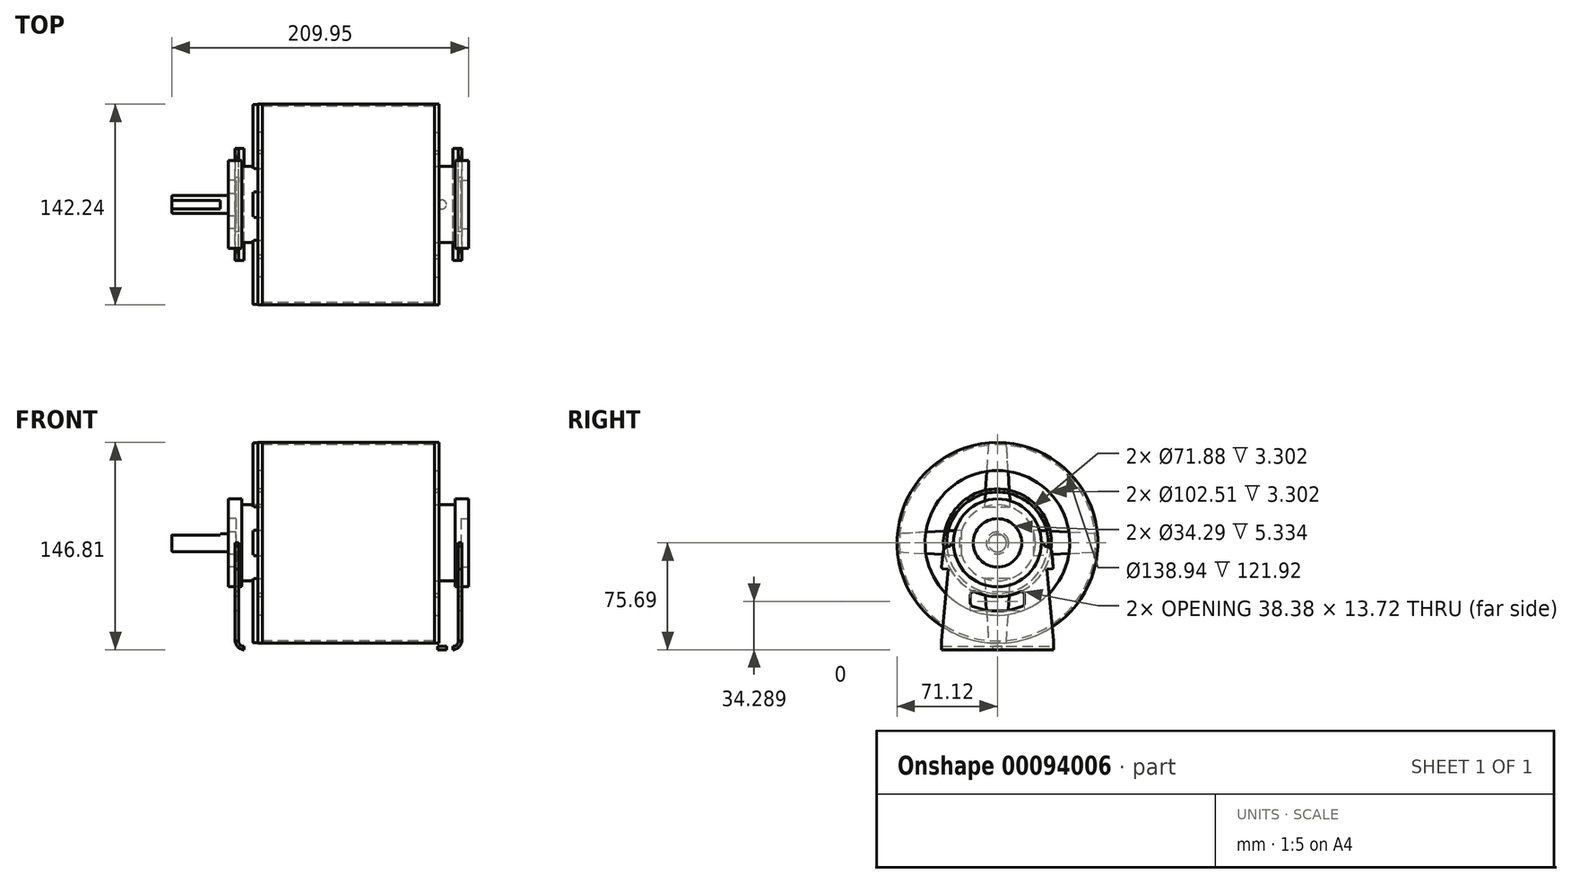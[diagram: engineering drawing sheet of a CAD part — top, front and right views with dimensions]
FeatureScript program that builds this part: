
annotation { "Feature Type Name" : "Feature", "Feature Type Description" : "" }
export const myFeature = defineFeature(function(context is Context, id is Id, definition is map)
    precondition{}
    {
        {
            var Q0;
            Q0=qCreatedBy(makeId("Right.planeOp"),FACE);
            var sketch = newSketch(context, id + "F0", { "sketchPlane" : qUnion([Q0])});
            skCircle(sketch, "E0", {"center": v(0, 0) * mm, "radius": 71.12 * mm});
            skCircle(sketch, "E1.0", {"center": v(0, 0) * mm, "radius": 69.47 * mm});
            skSolve(sketch);
        }
        {
            var Q0;
            Q0=makeQuery(id+"F0.imprint","IMPRINT",FACE,{"disambiguationData":[TD([[makeQuery(id+"F0.imprint","IMPRINT",EDGE,{"derivedFrom":sQuery(id+"F0.wireOp",EDGE,"E0")}),1.0]])]});
            extrude(context, id + "F1", {"entities" : qUnion([Q0]), "depth" : 121.92 * mm});
        }
        {
            var Q0;
            Q0=qCreatedBy(makeId("Front.planeOp"),FACE);
            var sketch = newSketch(context, id + "F2", { "sketchPlane" : qUnion([Q0])});
            skLineSegment(sketch, "E2", {"start": v(0, 0) * mm, "end": v(0, 71.12) * mm});
            skLineSegment(sketch, "E3", {"start": v(0, 71.12) * mm, "end": v(-3.3, 71.12) * mm});
            skLineSegment(sketch, "E4", {"start": v(-3.3, 71.12) * mm, "end": v(-3.3, 26.92) * mm});
            skLineSegment(sketch, "E5", {"start": v(-3.3, 26.92) * mm, "end": v(-14.48, 26.92) * mm});
            skLineSegment(sketch, "E6", {"start": v(-14.48, 26.92) * mm, "end": v(-14.48, 31.12) * mm});
            skLineSegment(sketch, "E7", {"start": v(-14.48, 31.12) * mm, "end": v(-24, 31.12) * mm});
            skLineSegment(sketch, "E8", {"start": v(-24, 31.12) * mm, "end": v(-24, 17.15) * mm});
            skLineSegment(sketch, "E9", {"start": v(-24, 17.15) * mm, "end": v(-18.67, 17.15) * mm});
            skLineSegment(sketch, "E10", {"start": v(-18.67, 17.15) * mm, "end": v(-18.67, 0) * mm});
            skLineSegment(sketch, "E11", {"start": v(-18.67, 0) * mm, "end": v(0, 0) * mm});
            skSolve(sketch);
        }
        {
            var Q0;
            Q0=makeQuery(id+"F2.imprint","IMPRINT",FACE,{"disambiguationData":[TD([[makeQuery(id+"F2.imprint","IMPRINT",EDGE,{"derivedFrom":sQuery(id+"F2.wireOp",EDGE,"E2")}),1.0]])]});
            var Q1;
            Q1=sQuery(id+"F2.wireOp",EDGE,"E11");
            revolve(context, id + "F3", {"entities" : qUnion([Q0]), "axis" : qUnion([Q1]), "revolveType" : RevolveType.FULL});
        }
        {
            var Q0;
            Q0=makeQuery(id+"F3.opRevolve","SWEPT_FACE",FACE,{"disambiguationData":[OSD([sQuery(id+"F2.wireOp",EDGE,"E4")])]});
            var sketch = newSketch(context, id + "F4", { "sketchPlane" : qUnion([Q0])});
            skCircle(sketch, "E12", {"center": v(0, 0) * mm, "radius": 51.26 * mm});
            skCircle(sketch, "E13", {"center": v(0, 0) * mm, "radius": 38.23 * mm});
            skCircle(sketch, "E14.0", {"center": v(0, 0) * mm, "radius": 35.94 * mm});
            skSolve(sketch);
        }
        {
            var Q0;
            Q0=qSketchRegion(id+"F4",true);
            var Q1;
            Q1=makeQuery(id+"F4.imprint","IMPRINT",FACE,{"disambiguationData":[TD([[makeQuery(id+"F4.imprint","IMPRINT",EDGE,{"derivedFrom":sQuery(id+"F4.wireOp",EDGE,"E14.0")}),1.0]])]});
            extrude(context, id + "F5", {"entities" : qUnion([Q0, Q1]), "operationType" : NewBodyOperationType.REMOVE, "endBound" : BoundingType.THROUGH_ALL, "oppositeDirection" : true, "depth" : 25.4 * mm});
        }
        {
            var Q0;
            Q0=qCreatedBy(makeId("Right.planeOp"),FACE);
            var sketch = newSketch(context, id + "F6", { "sketchPlane" : qUnion([Q0])});
            skLineSegment(sketch, "E15", {"start": v(0, 0) * mm, "end": v(0, 71.12) * mm, "construction": true});
            skPoint(sketch, "E16.rect.middle", {"position": v(0, 71.12) * mm});
            skCircle(sketch, "E17", {"center": v(0, 26.92) * mm, "radius": 9.2 * mm, "construction": true});
            skCircle(sketch, "E18.0", {"center": v(0, 0) * mm, "radius": 71.12 * mm, "construction": true});
            skCircle(sketch, "E19", {"center": v(0, 71.12) * mm, "radius": 6.35 * mm, "construction": true});
            skLineSegment(sketch, "E20", {"start": v(9.07, 25.35) * mm, "end": v(6.38, 70.83) * mm});
            skLineSegment(sketch, "E21", {"start": v(6.38, 70.83) * mm, "end": v(-6.38, 70.83) * mm});
            skLineSegment(sketch, "E22", {"start": v(-6.38, 70.83) * mm, "end": v(-9.07, 25.35) * mm});
            skLineSegment(sketch, "E23", {"start": v(-9.07, 25.35) * mm, "end": v(9.07, 25.35) * mm});
            skCircle(sketch, "E24.0", {"center": v(0, 0) * mm, "radius": 26.92 * mm, "construction": true});
            skSolve(sketch);
        }
        {
            var Q0;
            {var subQ3=sQuery(id+"F6.wireOp",EDGE,"E20");Q0=makeQuery(id+"F6.imprint","IMPRINT",FACE,{"disambiguationData":[TD([[makeQuery(id+"F6.imprint","IMPRINT",EDGE,{"derivedFrom":subQ3}),1.0]])]});}
            extrude(context, id + "F7", {"entities" : qUnion([Q0]), "oppositeDirection" : true, "depth" : 6.6 * mm});
        }
        {
            var Q0;
            Q0=makeQuery(id+"F7.opExtrude","CAP_EDGE",EDGE,{"disambiguationData":[OSD([sQuery(id+"F6.wireOp",EDGE,"E20")])],"isStart":false});
            var Q1;
            Q1=makeQuery(id+"F7.opExtrude","CAP_EDGE",EDGE,{"disambiguationData":[OSD([sQuery(id+"F6.wireOp",EDGE,"E21")])],"isStart":false});
            var Q2;
            Q2=makeQuery(id+"F7.opExtrude","CAP_EDGE",EDGE,{"disambiguationData":[OSD([sQuery(id+"F6.wireOp",EDGE,"E22")])],"isStart":false});
            var Q3;
            Q3=makeQuery(id+"F7.opExtrude","SWEPT_EDGE",EDGE,{"disambiguationData":[OSD([sQuery(id+"F2.wireOp",EDGE,"E3"),sQuery(id+"F2.wireOp",EDGE,"E4"),sQuery(id+"F6.wireOp",EDGE,"E20"),sQuery(id+"F6.wireOp",EDGE,"E21")])]});
            var Q4;
            Q4=makeQuery(id+"F7.opExtrude","SWEPT_EDGE",EDGE,{"disambiguationData":[OSD([sQuery(id+"F2.wireOp",EDGE,"E3"),sQuery(id+"F2.wireOp",EDGE,"E4"),sQuery(id+"F6.wireOp",EDGE,"E21"),sQuery(id+"F6.wireOp",EDGE,"E22")])]});
            fillet(context, id + "F8", {"entities" : qUnion([Q0, Q1, Q2, Q3, Q4]), "radius" : 0.5 * mm, "tangentPropagation" : true, "allowEdgeOverflow" : false});
        }
        {
            var Q0;
            Q0=makeQuery(id+"F7.opExtrude","SWEPT_BODY",BODY,{"disambiguationData":[OSD([sQuery(id+"F2.wireOp",EDGE,"E4"),sQuery(id+"F2.wireOp",EDGE,"E5"),sQuery(id+"F6.wireOp",EDGE,"E20"),sQuery(id+"F6.wireOp",EDGE,"E21"),sQuery(id+"F6.wireOp",EDGE,"E22")])]});
            var Q1;
            Q1=sQuery(id+"F2.wireOp",EDGE,"E11");
            circularPattern(context, id + "F9", {"entities" : qUnion([Q0]), "axis" : qUnion([Q1]), "angle" : 360 * degree, "instanceCount" : 4, "equalSpace" : true});
        }
        {
            var Q0;
            Q0=qCreatedBy(makeId("Right.planeOp"),FACE);
            cPlane(context, id + "F10", {"entities" : qUnion([Q0]), "cplaneType" : CPlaneType.OFFSET, "offset" : 60.96 * mm, "width" : 152.4 * mm, "height" : 152.4 * mm});
        }
        {
            var Q0;
            Q0=makeQuery(id+"F5.boolean.opBoolean","SPLIT",BODY,{"disambiguationData":[OD(0.0)],"derivedFrom":makeQuery(id+"F3.opRevolve","SWEPT_BODY",BODY,{"disambiguationData":[OSD([sQuery(id+"F2.wireOp",EDGE,"E2"),sQuery(id+"F2.wireOp",EDGE,"E3"),sQuery(id+"F2.wireOp",EDGE,"E4"),sQuery(id+"F2.wireOp",EDGE,"E5"),sQuery(id+"F2.wireOp",EDGE,"E6"),sQuery(id+"F2.wireOp",EDGE,"E7"),sQuery(id+"F2.wireOp",EDGE,"E8"),sQuery(id+"F2.wireOp",EDGE,"E9"),sQuery(id+"F2.wireOp",EDGE,"E10"),sQuery(id+"F2.wireOp",EDGE,"E11")])]})});
            var Q1;
            Q1=qCreatedBy(id+"F10.planeOp",FACE);
            mirror(context, id + "F11", {"entities" : qUnion([Q0]), "mirrorPlane" : qUnion([Q1])});
        }
        {
            var Q0;
            Q0=qCreatedBy(makeId("Front.planeOp"),FACE);
            var sketch = newSketch(context, id + "F12", { "sketchPlane" : qUnion([Q0])});
            skLineSegment(sketch, "E25.0.0", {"start": v(-18.67, -17.15) * mm, "end": v(-18.67, 17.15) * mm, "construction": true});
            skLineSegment(sketch, "E26", {"start": v(-18.67, 0) * mm, "end": v(-64.03, 0) * mm});
            skLineSegment(sketch, "E27", {"start": v(-64.03, 0) * mm, "end": v(-64.03, 5.84) * mm});
            skLineSegment(sketch, "E28", {"start": v(-63.53, 6.35) * mm, "end": v(-23.75, 6.35) * mm});
            skLineSegment(sketch, "E29", {"start": v(-23.24, 7.89) * mm, "end": v(-18.67, 7.89) * mm});
            skLineSegment(sketch, "E30", {"start": v(-18.67, 7.89) * mm, "end": v(-18.67, 0) * mm});
            skLineSegment(sketch, "E31", {"start": v(-23.75, 7.38) * mm, "end": v(-23.75, 6.35) * mm});
            skPoint(sketch, "E32.visualSharp", {"position": v(-23.75, 7.89) * mm});
            skArc(sketch, "E32.filletArc", {"start": v(-23.24, 7.89) * mm, "mid": v(-23.6, 7.74) * mm, "end": v(-23.75, 7.38) * mm});
            skPoint(sketch, "E33.visualSharp", {"position": v(-64.03, 6.35) * mm});
            skArc(sketch, "E33.filletArc", {"start": v(-63.53, 6.35) * mm, "mid": v(-63.88, 6.2) * mm, "end": v(-64.03, 5.84) * mm});
            skSolve(sketch);
        }
        {
            var Q0;
            Q0=makeQuery(id+"F12.imprint","IMPRINT",FACE,{"disambiguationData":[TD([[makeQuery(id+"F12.imprint","IMPRINT",EDGE,{"derivedFrom":sQuery(id+"F12.wireOp",EDGE,"E26")}),-1.0]])]});
            var Q1;
            Q1=sQuery(id+"F12.wireOp",EDGE,"E26");
            revolve(context, id + "F13", {"entities" : qUnion([Q0]), "axis" : qUnion([Q1]), "revolveType" : RevolveType.FULL});
        }
        {
            var Q0;
            Q0=makeQuery(id+"F13.opRevolve","SWEPT_FACE",FACE,{"disambiguationData":[OSD([sQuery(id+"F12.wireOp",EDGE,"E27")])]});
            var sketch = newSketch(context, id + "F14", { "sketchPlane" : qUnion([Q0])});
            skCircle(sketch, "E34.0", {"center": v(0, 0) * mm, "radius": 6.35 * mm});
            skLineSegment(sketch, "E35", {"start": v(-6.6, -6.35) * mm, "end": v(6.6, -6.35) * mm, "construction": true});
            skLineSegment(sketch, "E36", {"start": v(0, -6.35) * mm, "end": v(0, 6.35) * mm, "construction": true});
            skLineSegment(sketch, "E37.0", {"start": v(-3.02, 5.59) * mm, "end": v(3.02, 5.59) * mm});
            skSolve(sketch);
        }
        {
            var Q0;
            {var subQ0=makeQuery(id+"F13.opRevolve","SWEPT_EDGE",EDGE,{"disambiguationData":[OSD([sQuery(id+"F12.wireOp",EDGE,"E27"),sQuery(id+"F12.wireOp",EDGE,"E33.filletArc")])]});var subQ1=sQuery(id+"F14.wireOp",EDGE,"E37.0");var subQ3=makeQuery(id+"F14.imprint","INTERSECT",VERTEX,{"disambiguationData":[OD(0.0)],"derivedFrom":[subQ0,subQ1]});Q0=makeQuery(id+"F14.imprint","IMPRINT",FACE,{"disambiguationData":[TD([[makeQuery(id+"F14.imprint","IMPRINT",EDGE,{"disambiguationData":[TD([[subQ3,-1.0]])],"derivedFrom":subQ1}),1.0]])]});}
            var Q1;
            {var subQ1=sQuery(id+"F14.wireOp",EDGE,"E37.0");var subQ4=sQuery(id+"F14.wireOp",EDGE,"E34.0");var subQ6=makeQuery(id+"F14.imprint","INTERSECT",VERTEX,{"disambiguationData":[OD(0.0)],"derivedFrom":[subQ4,subQ1]});Q1=makeQuery(id+"F14.imprint","IMPRINT",FACE,{"disambiguationData":[TD([[makeQuery(id+"F14.imprint","IMPRINT",EDGE,{"disambiguationData":[TD([[subQ6,1.0]])],"derivedFrom":subQ4}),1.0]])]});}
            extrude(context, id + "F15", {"entities" : qUnion([Q0, Q1]), "operationType" : NewBodyOperationType.REMOVE, "oppositeDirection" : true, "depth" : 34.04 * mm});
        }
        {
            var Q0;
            Q0=qCreatedBy(makeId("Front.planeOp"),FACE);
            var sketch = newSketch(context, id + "F16", { "sketchPlane" : qUnion([Q0])});
            skLineSegment(sketch, "E38", {"start": v(-154.25, 0) * mm, "end": v(252.33, 0) * mm, "construction": true});
            skLineSegment(sketch, "E39", {"start": v(-12.9, -75.7) * mm, "end": v(134.81, -75.7) * mm});
            skLineSegment(sketch, "E40", {"start": v(-24, 31.12) * mm, "end": v(-14.48, 31.12) * mm, "construction": true});
            skLineSegment(sketch, "E41", {"start": v(136.4, 31.12) * mm, "end": v(145.92, 31.12) * mm, "construction": true});
            skLineSegment(sketch, "E42", {"start": v(-19.24, 31.12) * mm, "end": v(-19.24, 0) * mm, "construction": true});
            skLineSegment(sketch, "E43", {"start": v(141.16, 31.12) * mm, "end": v(141.16, 0) * mm, "construction": true});
            skLineSegment(sketch, "E44", {"start": v(-19.24, 0) * mm, "end": v(-19.24, -69.34) * mm});
            skLineSegment(sketch, "E45", {"start": v(141.16, 0) * mm, "end": v(141.16, -69.34) * mm});
            skPoint(sketch, "E46.visualSharp", {"position": v(-19.24, -75.7) * mm});
            skArc(sketch, "E46.filletArc", {"start": v(-19.24, -69.34) * mm, "mid": v(-17.38, -73.83) * mm, "end": v(-12.9, -75.7) * mm});
            skPoint(sketch, "E47.visualSharp", {"position": v(141.16, -75.7) * mm});
            skArc(sketch, "E47.filletArc", {"start": v(134.81, -75.7) * mm, "mid": v(139.3, -73.83) * mm, "end": v(141.16, -69.34) * mm});
            skLineSegment(sketch, "E48.0", {"start": v(138.87, 0) * mm, "end": v(138.87, -69.34) * mm});
            skArc(sketch, "E48.1", {"start": v(134.81, -73.4) * mm, "mid": v(137.68, -72.22) * mm, "end": v(138.87, -69.34) * mm});
            skLineSegment(sketch, "E48.2", {"start": v(-12.9, -73.4) * mm, "end": v(134.81, -73.4) * mm});
            skArc(sketch, "E48.3", {"start": v(-16.95, -69.34) * mm, "mid": v(-15.76, -72.22) * mm, "end": v(-12.9, -73.4) * mm});
            skLineSegment(sketch, "E48.4", {"start": v(-16.95, 0) * mm, "end": v(-16.95, -69.34) * mm});
            skLineSegment(sketch, "E49", {"start": v(-19.24, 0) * mm, "end": v(-16.95, 0) * mm});
            skLineSegment(sketch, "E50", {"start": v(138.87, 0) * mm, "end": v(141.16, 0) * mm});
            skSolve(sketch);
        }
        {
            var Q0;
            Q0=qSketchRegion(id+"F16",true);
            extrude(context, id + "F17", {"entities" : qUnion([Q0]), "endBound" : BoundingType.SYMMETRIC, "depth" : 79.5 * mm});
        }
        {
            var Q0;
            Q0=qCreatedBy(makeId("Top.planeOp"),FACE);
            cPlane(context, id + "F18", {"entities" : qUnion([Q0]), "cplaneType" : CPlaneType.OFFSET, "offset" : 75.7 * mm, "oppositeDirection" : true, "width" : 152.4 * mm, "height" : 152.4 * mm});
        }
        {
            var Q0;
            Q0=qCreatedBy(id+"F18.planeOp",FACE);
            var sketch = newSketch(context, id + "F19", { "sketchPlane" : qUnion([Q0])});
            skLineSegment(sketch, "E51.0", {"start": v(-19.24, -39.75) * mm, "end": v(-12.9, -39.75) * mm, "construction": true});
            skLineSegment(sketch, "E52.0", {"start": v(-19.24, 39.75) * mm, "end": v(-12.9, 39.75) * mm, "construction": true});
            skLineSegment(sketch, "E53.bottom", {"start": v(15.34, 66.04) * mm, "end": v(15.34, 66.04) * mm});
            skLineSegment(sketch, "E53.top", {"start": v(15.34, 40.64) * mm, "end": v(15.34, 40.64) * mm});
            skLineSegment(sketch, "E53.left", {"start": v(11.37, 62.07) * mm, "end": v(11.37, 44.6) * mm});
            skLineSegment(sketch, "E53.right", {"start": v(19.3, 62.07) * mm, "end": v(19.3, 44.6) * mm});
            skPoint(sketch, "E54.visualSharp", {"position": v(11.37, 66.04) * mm});
            skArc(sketch, "E54.filletArc", {"start": v(15.34, 66.04) * mm, "mid": v(12.53, 64.88) * mm, "end": v(11.37, 62.07) * mm});
            skPoint(sketch, "E55.visualSharp", {"position": v(19.3, 66.04) * mm});
            skArc(sketch, "E55.filletArc", {"start": v(19.3, 62.07) * mm, "mid": v(18.14, 64.88) * mm, "end": v(15.34, 66.04) * mm});
            skPoint(sketch, "E56.visualSharp", {"position": v(19.3, 40.64) * mm});
            skArc(sketch, "E56.filletArc", {"start": v(15.34, 40.64) * mm, "mid": v(18.14, 41.8) * mm, "end": v(19.3, 44.6) * mm});
            skPoint(sketch, "E57.visualSharp", {"position": v(11.37, 40.64) * mm});
            skArc(sketch, "E57.filletArc", {"start": v(11.37, 44.6) * mm, "mid": v(12.53, 41.8) * mm, "end": v(15.34, 40.64) * mm});
            skLineSegment(sketch, "E58", {"start": v(2.98, 39.75) * mm, "end": v(2.98, -39.75) * mm, "construction": true});
            skLineSegment(sketch, "E59", {"start": v(-19.24, 0) * mm, "end": v(141.16, 0) * mm, "construction": true});
            skLineSegment(sketch, "E60", {"start": v(9.33, 71.5) * mm, "end": v(111.68, 71.5) * mm});
            skLineSegment(sketch, "E61", {"start": v(9.33, -71.5) * mm, "end": v(111.68, -71.5) * mm});
            skLineSegment(sketch, "E62", {"start": v(2.98, 46.1) * mm, "end": v(2.98, 65.15) * mm});
            skLineSegment(sketch, "E63", {"start": v(2.98, -46.1) * mm, "end": v(2.98, -65.15) * mm});
            skLineSegment(sketch, "E64", {"start": v(-19.24, 39.75) * mm, "end": v(-19.24, -39.75) * mm, "construction": true});
            skLineSegment(sketch, "E65.0", {"start": v(141.16, -39.75) * mm, "end": v(141.16, 39.75) * mm, "construction": true});
            skLineSegment(sketch, "E66", {"start": v(141.16, 39.75) * mm, "end": v(134.81, 39.75) * mm, "construction": true});
            skLineSegment(sketch, "E67", {"start": v(126.25, 45.4) * mm, "end": v(117.6, 67.47) * mm});
            skPoint(sketch, "E68.visualSharp", {"position": v(128.46, 39.75) * mm});
            skArc(sketch, "E68.filletArc", {"start": v(126.25, 45.4) * mm, "mid": v(129.51, 41.3) * mm, "end": v(134.52, 39.75) * mm});
            skPoint(sketch, "E69.visualSharp", {"position": v(2.98, 71.5) * mm});
            skArc(sketch, "E69.filletArc", {"start": v(9.33, 71.5) * mm, "mid": v(4.84, 69.64) * mm, "end": v(2.98, 65.15) * mm});
            skLineSegment(sketch, "E70.0.MirrorCS", {"start": v(141.16, -39.75) * mm, "end": v(134.81, -39.75) * mm, "construction": true});
            skLineSegment(sketch, "E70.1.MirrorCS", {"start": v(126.25, -45.4) * mm, "end": v(117.6, -67.47) * mm});
            skArc(sketch, "E70.2.MirrorCS", {"start": v(126.25, -45.4) * mm, "mid": v(129.51, -41.3) * mm, "end": v(134.52, -39.75) * mm});
            skPoint(sketch, "E71.visualSharp", {"position": v(116.01, 71.5) * mm});
            skArc(sketch, "E71.filletArc", {"start": v(117.6, 67.47) * mm, "mid": v(115.26, 70.4) * mm, "end": v(111.68, 71.5) * mm});
            skPoint(sketch, "E72.visualSharp", {"position": v(116.01, -71.5) * mm});
            skArc(sketch, "E72.filletArc", {"start": v(111.68, -71.5) * mm, "mid": v(115.26, -70.4) * mm, "end": v(117.6, -67.47) * mm});
            skPoint(sketch, "E73.visualSharp", {"position": v(2.98, -71.5) * mm});
            skArc(sketch, "E73.filletArc", {"start": v(2.98, -65.15) * mm, "mid": v(4.84, -69.64) * mm, "end": v(9.33, -71.5) * mm});
            skPoint(sketch, "E74.visualSharp", {"position": v(2.98, 39.75) * mm});
            skArc(sketch, "E74.filletArc", {"start": v(-3.37, 39.75) * mm, "mid": v(1.12, 41.61) * mm, "end": v(2.98, 46.1) * mm});
            skPoint(sketch, "E75.visualSharp", {"position": v(2.98, -39.75) * mm});
            skArc(sketch, "E75.filletArc", {"start": v(2.98, -46.1) * mm, "mid": v(1.12, -41.61) * mm, "end": v(-3.37, -39.75) * mm});
            skArc(sketch, "E76.0.1.0", {"start": v(15.34, -66.04) * mm, "mid": v(18.14, -64.88) * mm, "end": v(19.3, -62.07) * mm});
            skArc(sketch, "E76.0.1.1", {"start": v(11.37, -62.07) * mm, "mid": v(12.53, -64.88) * mm, "end": v(15.34, -66.04) * mm});
            skLineSegment(sketch, "E76.0.1.2", {"start": v(11.37, -44.6) * mm, "end": v(11.37, -62.07) * mm});
            skArc(sketch, "E76.0.1.3", {"start": v(15.34, -40.64) * mm, "mid": v(12.53, -41.8) * mm, "end": v(11.37, -44.6) * mm});
            skArc(sketch, "E76.0.1.4", {"start": v(19.3, -44.6) * mm, "mid": v(18.14, -41.8) * mm, "end": v(15.34, -40.64) * mm});
            skLineSegment(sketch, "E76.0.1.5", {"start": v(19.3, -44.6) * mm, "end": v(19.3, -62.07) * mm});
            skArc(sketch, "E76.1.0.0", {"start": v(83.92, 40.64) * mm, "mid": v(86.72, 41.8) * mm, "end": v(87.88, 44.6) * mm});
            skArc(sketch, "E76.1.0.1", {"start": v(79.95, 44.6) * mm, "mid": v(81.1, 41.8) * mm, "end": v(83.92, 40.64) * mm});
            skLineSegment(sketch, "E76.1.0.2", {"start": v(79.95, 62.07) * mm, "end": v(79.95, 44.6) * mm});
            skArc(sketch, "E76.1.0.3", {"start": v(83.92, 66.04) * mm, "mid": v(81.1, 64.88) * mm, "end": v(79.95, 62.07) * mm});
            skArc(sketch, "E76.1.0.4", {"start": v(87.88, 62.07) * mm, "mid": v(86.72, 64.88) * mm, "end": v(83.92, 66.04) * mm});
            skLineSegment(sketch, "E76.1.0.5", {"start": v(87.88, 62.07) * mm, "end": v(87.88, 44.6) * mm});
            skArc(sketch, "E76.1.1.0", {"start": v(83.92, -66.04) * mm, "mid": v(86.72, -64.88) * mm, "end": v(87.88, -62.07) * mm});
            skArc(sketch, "E76.1.1.1", {"start": v(79.95, -62.07) * mm, "mid": v(81.1, -64.88) * mm, "end": v(83.92, -66.04) * mm});
            skLineSegment(sketch, "E76.1.1.2", {"start": v(79.95, -44.6) * mm, "end": v(79.95, -62.07) * mm});
            skArc(sketch, "E76.1.1.3", {"start": v(83.92, -40.64) * mm, "mid": v(81.1, -41.8) * mm, "end": v(79.95, -44.6) * mm});
            skArc(sketch, "E76.1.1.4", {"start": v(87.88, -44.6) * mm, "mid": v(86.72, -41.8) * mm, "end": v(83.92, -40.64) * mm});
            skLineSegment(sketch, "E76.1.1.5", {"start": v(87.88, -44.6) * mm, "end": v(87.88, -62.07) * mm});
            skLineSegment(sketch, "E76.direction1", {"start": v(15.34, 40.64) * mm, "end": v(83.92, 40.64) * mm, "construction": true});
            skLineSegment(sketch, "E76.direction2", {"start": v(15.34, 40.64) * mm, "end": v(15.34, -66.04) * mm, "construction": true});
            skLineSegment(sketch, "E77.0", {"start": v(-12.9, -39.75) * mm, "end": v(-12.9, 39.75) * mm});
            skLineSegment(sketch, "E78.0", {"start": v(134.81, -39.75) * mm, "end": v(134.81, 39.75) * mm});
            skLineSegment(sketch, "E79", {"start": v(-12.9, 39.75) * mm, "end": v(-3.37, 39.75) * mm});
            skLineSegment(sketch, "E80", {"start": v(-12.9, -39.75) * mm, "end": v(-3.37, -39.75) * mm});
            skLineSegment(sketch, "E81", {"start": v(134.81, 39.75) * mm, "end": v(134.52, 39.75) * mm});
            skLineSegment(sketch, "E82", {"start": v(134.81, -39.75) * mm, "end": v(134.52, -39.75) * mm});
            skSolve(sketch);
        }
        {
            var Q0;
            Q0=makeQuery(id+"F19.imprint","IMPRINT",FACE,{"disambiguationData":[TD([[makeQuery(id+"F19.imprint","IMPRINT",EDGE,{"derivedFrom":sQuery(id+"F19.wireOp",EDGE,"E53.left")}),-1.0]])]});
            extrude(context, id + "F20", {"entities" : qUnion([Q0]), "operationType" : NewBodyOperationType.ADD, "depth" : 2.3 * mm});
        }
        {
            var Q0;
            Q0=makeQuery(id+"F17.opExtrude","SWEPT_FACE",FACE,{"disambiguationData":[OSD([sQuery(id+"F16.wireOp",EDGE,"E44")])]});
            var sketch = newSketch(context, id + "F21", { "sketchPlane" : qUnion([Q0])});
            skArc(sketch, "E83.0", {"start": v(-31.12, 0) * mm, "mid": v(0, -31.12) * mm, "end": v(31.12, 0) * mm});
            skLineSegment(sketch, "E84.0", {"start": v(39.75, -69.34) * mm, "end": v(-39.75, -69.34) * mm});
            skLineSegment(sketch, "E85", {"start": v(31.87, 0) * mm, "end": v(31.12, 0) * mm});
            skLineSegment(sketch, "E86", {"start": v(-33.13, -1.15) * mm, "end": v(-39.75, -69.34) * mm});
            skLineSegment(sketch, "E87", {"start": v(33.13, -1.15) * mm, "end": v(39.75, -69.34) * mm});
            skPoint(sketch, "E88.end.orphan", {"position": v(-39.75, 0) * mm});
            skPoint(sketch, "E89.0.start.orphan", {"position": v(39.75, 0) * mm});
            skLineSegment(sketch, "E90.trimOffspring", {"start": v(-31.12, 0) * mm, "end": v(-31.87, 0) * mm});
            skLineSegment(sketch, "E91", {"start": v(0, 0) * mm, "end": v(0, -69.34) * mm, "construction": true});
            skPoint(sketch, "E92.visualSharp", {"position": v(-33.02, 0) * mm});
            skArc(sketch, "E92.filletArc", {"start": v(-31.87, 0) * mm, "mid": v(-32.72, -0.33) * mm, "end": v(-33.13, -1.15) * mm});
            skPoint(sketch, "E93.visualSharp", {"position": v(33.02, 0) * mm});
            skArc(sketch, "E93.filletArc", {"start": v(33.13, -1.15) * mm, "mid": v(32.72, -0.33) * mm, "end": v(31.87, 0) * mm});
            skLineSegment(sketch, "E94.bottom", {"start": v(33.27, -2.6) * mm, "end": v(33.78, -2.55) * mm});
            skLineSegment(sketch, "E94.top", {"start": v(34.84, -18.78) * mm, "end": v(38.38, -18.44) * mm});
            skLineSegment(sketch, "E94.left", {"start": v(33.27, -2.6) * mm, "end": v(34.84, -18.78) * mm});
            skLineSegment(sketch, "E94.right", {"start": v(38.5, -6.43) * mm, "end": v(39.52, -17.05) * mm});
            skPoint(sketch, "E95.visualSharp", {"position": v(38.08, -2.13) * mm});
            skArc(sketch, "E95.filletArc", {"start": v(38.5, -6.43) * mm, "mid": v(36.94, -3.51) * mm, "end": v(33.78, -2.55) * mm});
            skPoint(sketch, "E96.visualSharp", {"position": v(39.65, -18.31) * mm});
            skArc(sketch, "E96.filletArc", {"start": v(38.38, -18.44) * mm, "mid": v(39.24, -17.98) * mm, "end": v(39.52, -17.05) * mm});
            skLineSegment(sketch, "E97.0.MirrorCS", {"start": v(-33.27, -2.6) * mm, "end": v(-33.78, -2.55) * mm});
            skArc(sketch, "E97.1.MirrorCS", {"start": v(-38.5, -6.43) * mm, "mid": v(-36.94, -3.51) * mm, "end": v(-33.78, -2.55) * mm});
            skLineSegment(sketch, "E97.2.MirrorCS", {"start": v(-34.84, -18.78) * mm, "end": v(-38.38, -18.44) * mm});
            skLineSegment(sketch, "E97.3.MirrorCS", {"start": v(-38.5, -6.43) * mm, "end": v(-39.52, -17.05) * mm});
            skArc(sketch, "E97.4.MirrorCS", {"start": v(-38.38, -18.44) * mm, "mid": v(-39.24, -17.98) * mm, "end": v(-39.52, -17.05) * mm});
            skArc(sketch, "E98", {"start": v(-15.6, -34.76) * mm, "mid": v(0, -38.1) * mm, "end": v(15.6, -34.76) * mm});
            skArc(sketch, "E99.0", {"start": v(-17.57, -44.95) * mm, "mid": v(0, -48.26) * mm, "end": v(17.57, -44.95) * mm});
            skLineSegment(sketch, "E100.rect.left", {"start": v(19.19, -37.07) * mm, "end": v(19.19, -42.58) * mm});
            skLineSegment(sketch, "E100.rect.right", {"start": v(-19.19, -37.07) * mm, "end": v(-19.19, -42.58) * mm});
            skPoint(sketch, "E100.rect.middle", {"position": v(0, -43.18) * mm});
            skPoint(sketch, "E101.orphan", {"position": v(-19.19, -53.44) * mm});
            skPoint(sketch, "E100.rect.top.start.orphan", {"position": v(19.19, -53.44) * mm});
            skPoint(sketch, "E102.visualSharp", {"position": v(-19.19, -44.28) * mm});
            skArc(sketch, "E102.filletArc", {"start": v(-19.19, -42.58) * mm, "mid": v(-18.75, -44.01) * mm, "end": v(-17.57, -44.95) * mm});
            skPoint(sketch, "E103.visualSharp", {"position": v(19.19, -44.28) * mm});
            skArc(sketch, "E103.filletArc", {"start": v(17.57, -44.95) * mm, "mid": v(18.75, -44.01) * mm, "end": v(19.19, -42.58) * mm});
            skPoint(sketch, "E104.visualSharp", {"position": v(19.19, -32.92) * mm});
            skArc(sketch, "E104.filletArc", {"start": v(19.19, -37.07) * mm, "mid": v(18.03, -34.94) * mm, "end": v(15.6, -34.76) * mm});
            skPoint(sketch, "E105.visualSharp", {"position": v(-19.19, -32.92) * mm});
            skArc(sketch, "E105.filletArc", {"start": v(-15.6, -34.76) * mm, "mid": v(-18.03, -34.94) * mm, "end": v(-19.19, -37.07) * mm});
            skSolve(sketch);
        }
        {
            var Q0;
            {var subQ2=sQuery(id+"F21.wireOp",EDGE,"E92.filletArc");Q0=makeQuery(id+"F21.imprint","IMPRINT",FACE,{"disambiguationData":[TD([[makeQuery(id+"F21.imprint","IMPRINT",EDGE,{"derivedFrom":subQ2}),-1.0]])]});}
            var Q1;
            {var subQ2=sQuery(id+"F21.wireOp",EDGE,"E93.filletArc");Q1=makeQuery(id+"F21.imprint","IMPRINT",FACE,{"disambiguationData":[TD([[makeQuery(id+"F21.imprint","IMPRINT",EDGE,{"derivedFrom":subQ2}),-1.0]])]});}
            var Q2;
            {var subQ1=sQuery(id+"F21.wireOp",EDGE,"E83.0");Q2=makeQuery(id+"F21.imprint","IMPRINT",FACE,{"disambiguationData":[TD([[makeQuery(id+"F21.imprint","IMPRINT",EDGE,{"derivedFrom":subQ1}),1.0]])]});}
            var Q3;
            Q3=makeQuery(id+"F21.imprint","IMPRINT",FACE,{"disambiguationData":[TD([[makeQuery(id+"F21.imprint","IMPRINT",EDGE,{"derivedFrom":sQuery(id+"F21.wireOp",EDGE,"E98")}),-1.0]])]});
            extrude(context, id + "F22", {"entities" : qUnion([Q0, Q1, Q2, Q3]), "oppositeDirection" : true, "depth" : 160.4 * mm});
        }
        {
            var Q0;
            Q0=makeQuery(id+"F22.opExtrude","SWEPT_BODY",BODY,{"disambiguationData":[OSD([sQuery(id+"F16.wireOp",EDGE,"E44"),sQuery(id+"F16.wireOp",EDGE,"E49"),sQuery(id+"F21.wireOp",EDGE,"E83.0")])]});
            var Q1;
            Q1=makeQuery(id+"F22.opExtrude","SWEPT_BODY",BODY,{"disambiguationData":[OSD([sQuery(id+"F16.wireOp",EDGE,"E44"),sQuery(id+"F16.wireOp",EDGE,"E49"),sQuery(id+"F21.wireOp",EDGE,"E86"),sQuery(id+"F21.wireOp",EDGE,"E92.filletArc"),sQuery(id+"F21.wireOp",EDGE,"E97.0.MirrorCS"),sQuery(id+"F21.wireOp",EDGE,"E97.1.MirrorCS"),sQuery(id+"F21.wireOp",EDGE,"E97.2.MirrorCS"),sQuery(id+"F21.wireOp",EDGE,"E97.3.MirrorCS"),sQuery(id+"F21.wireOp",EDGE,"E97.4.MirrorCS")])]});
            var Q2;
            Q2=makeQuery(id+"F22.opExtrude","SWEPT_BODY",BODY,{"disambiguationData":[OSD([sQuery(id+"F16.wireOp",EDGE,"E44"),sQuery(id+"F16.wireOp",EDGE,"E49"),sQuery(id+"F21.wireOp",EDGE,"E87"),sQuery(id+"F21.wireOp",EDGE,"E93.filletArc"),sQuery(id+"F21.wireOp",EDGE,"E94.bottom"),sQuery(id+"F21.wireOp",EDGE,"E94.top"),sQuery(id+"F21.wireOp",EDGE,"E94.right"),sQuery(id+"F21.wireOp",EDGE,"E95.filletArc"),sQuery(id+"F21.wireOp",EDGE,"E96.filletArc")])]});
            var Q3;
            Q3=makeQuery(id+"F22.opExtrude","SWEPT_BODY",BODY,{"disambiguationData":[OSD([sQuery(id+"F21.wireOp",EDGE,"E98"),sQuery(id+"F21.wireOp",EDGE,"E99.0"),sQuery(id+"F21.wireOp",EDGE,"E100.rect.left"),sQuery(id+"F21.wireOp",EDGE,"E100.rect.right"),sQuery(id+"F21.wireOp",EDGE,"E102.filletArc"),sQuery(id+"F21.wireOp",EDGE,"E103.filletArc"),sQuery(id+"F21.wireOp",EDGE,"E104.filletArc"),sQuery(id+"F21.wireOp",EDGE,"E105.filletArc")])]});
            var Q4;
            Q4=makeQuery(id+"F17.opExtrude","SWEPT_BODY",BODY,{"disambiguationData":[OSD([sQuery(id+"F16.wireOp",EDGE,"E39"),sQuery(id+"F16.wireOp",EDGE,"E44"),sQuery(id+"F16.wireOp",EDGE,"E45"),sQuery(id+"F16.wireOp",EDGE,"E46.filletArc"),sQuery(id+"F16.wireOp",EDGE,"E47.filletArc"),sQuery(id+"F16.wireOp",EDGE,"E48.0"),sQuery(id+"F16.wireOp",EDGE,"E48.1"),sQuery(id+"F16.wireOp",EDGE,"E48.2"),sQuery(id+"F16.wireOp",EDGE,"E48.3"),sQuery(id+"F16.wireOp",EDGE,"E48.4"),sQuery(id+"F16.wireOp",EDGE,"E49"),sQuery(id+"F16.wireOp",EDGE,"E50")])]});
            booleanBodies(context, id + "F23", {"operationType" : BooleanOperationType.SUBTRACTION, "tools" : qUnion([Q0, Q1, Q2, Q3]), "targets" : qUnion([Q4])});
        }
        {
            var Q0;
            Q0=makeQuery(id+"F20.boolean.opBoolean","MERGE",FACE,{"derivedFrom":[makeQuery(id+"F17.opExtrude","SWEPT_FACE",FACE,{"disambiguationData":[OSD([sQuery(id+"F16.wireOp",EDGE,"E48.2")])]}),makeQuery(id+"F20.opExtrude","CAP_FACE",FACE,{"disambiguationData":[OSD([sQuery(id+"F19.wireOp",EDGE,"E53.left"),sQuery(id+"F19.wireOp",EDGE,"E53.right"),sQuery(id+"F19.wireOp",EDGE,"E54.filletArc"),sQuery(id+"F19.wireOp",EDGE,"E55.filletArc"),sQuery(id+"F19.wireOp",EDGE,"E56.filletArc"),sQuery(id+"F19.wireOp",EDGE,"E57.filletArc"),sQuery(id+"F19.wireOp",EDGE,"E60"),sQuery(id+"F19.wireOp",EDGE,"E61"),sQuery(id+"F19.wireOp",EDGE,"E62"),sQuery(id+"F19.wireOp",EDGE,"E63"),sQuery(id+"F19.wireOp",EDGE,"E67"),sQuery(id+"F19.wireOp",EDGE,"E68.filletArc"),sQuery(id+"F19.wireOp",EDGE,"E69.filletArc"),sQuery(id+"F19.wireOp",EDGE,"E70.1.MirrorCS"),sQuery(id+"F19.wireOp",EDGE,"E70.2.MirrorCS"),sQuery(id+"F19.wireOp",EDGE,"E71.filletArc"),sQuery(id+"F19.wireOp",EDGE,"E72.filletArc"),sQuery(id+"F19.wireOp",EDGE,"E73.filletArc"),sQuery(id+"F19.wireOp",EDGE,"E74.filletArc"),sQuery(id+"F19.wireOp",EDGE,"E75.filletArc"),sQuery(id+"F19.wireOp",EDGE,"E76.0.1.0"),sQuery(id+"F19.wireOp",EDGE,"E76.0.1.1"),sQuery(id+"F19.wireOp",EDGE,"E76.0.1.2"),sQuery(id+"F19.wireOp",EDGE,"E76.0.1.3"),sQuery(id+"F19.wireOp",EDGE,"E76.0.1.4"),sQuery(id+"F19.wireOp",EDGE,"E76.0.1.5"),sQuery(id+"F19.wireOp",EDGE,"E76.1.0.0"),sQuery(id+"F19.wireOp",EDGE,"E76.1.0.1"),sQuery(id+"F19.wireOp",EDGE,"E76.1.0.2"),sQuery(id+"F19.wireOp",EDGE,"E76.1.0.3"),sQuery(id+"F19.wireOp",EDGE,"E76.1.0.4"),sQuery(id+"F19.wireOp",EDGE,"E76.1.0.5"),sQuery(id+"F19.wireOp",EDGE,"E76.1.1.0"),sQuery(id+"F19.wireOp",EDGE,"E76.1.1.1"),sQuery(id+"F19.wireOp",EDGE,"E76.1.1.2"),sQuery(id+"F19.wireOp",EDGE,"E76.1.1.3"),sQuery(id+"F19.wireOp",EDGE,"E76.1.1.4"),sQuery(id+"F19.wireOp",EDGE,"E76.1.1.5"),sQuery(id+"F19.wireOp",EDGE,"E77.0"),sQuery(id+"F19.wireOp",EDGE,"E78.0"),sQuery(id+"F19.wireOp",EDGE,"E79"),sQuery(id+"F19.wireOp",EDGE,"E80"),sQuery(id+"F19.wireOp",EDGE,"E81"),sQuery(id+"F19.wireOp",EDGE,"E82")])],"isStart":false})]});
            var sketch = newSketch(context, id + "F24", { "sketchPlane" : qUnion([Q0])});
            skLineSegment(sketch, "E106.0", {"start": v(-12.9, -39.75) * mm, "end": v(-12.9, 39.75) * mm, "construction": true});
            skLineSegment(sketch, "E107.0", {"start": v(134.81, -39.75) * mm, "end": v(134.81, 39.75) * mm, "construction": true});
            skLineSegment(sketch, "E108.rect.bottom", {"start": v(4.89, 7.62) * mm, "end": v(117.03, 7.62) * mm});
            skLineSegment(sketch, "E108.rect.top", {"start": v(4.89, -7.62) * mm, "end": v(117.03, -7.62) * mm});
            skLineSegment(sketch, "E108.rect.left", {"start": v(2.35, 5.08) * mm, "end": v(2.35, -5.08) * mm});
            skLineSegment(sketch, "E108.rect.right", {"start": v(119.57, 5.08) * mm, "end": v(119.57, -5.08) * mm});
            skPoint(sketch, "E108.rect.middle", {"position": v(60.96, 0) * mm});
            skLineSegment(sketch, "E109", {"start": v(2.35, 0) * mm, "end": v(-12.9, 0) * mm, "construction": true});
            skLineSegment(sketch, "E110", {"start": v(119.57, 0) * mm, "end": v(134.81, 0) * mm, "construction": true});
            skCircle(sketch, "E111", {"center": v(-5.27, 0) * mm, "radius": 3.18 * mm});
            skLineSegment(sketch, "E112", {"start": v(60.96, 7.62) * mm, "end": v(60.96, -7.62) * mm, "construction": true});
            skCircle(sketch, "E113.0.MirrorC", {"center": v(127.2, 0) * mm, "radius": 3.18 * mm});
            skPoint(sketch, "E114.visualSharp", {"position": v(2.35, 7.62) * mm});
            skArc(sketch, "E114.filletArc", {"start": v(4.89, 7.62) * mm, "mid": v(3.1, 6.88) * mm, "end": v(2.35, 5.08) * mm});
            skPoint(sketch, "E115.visualSharp", {"position": v(119.57, 7.62) * mm});
            skArc(sketch, "E115.filletArc", {"start": v(119.57, 5.08) * mm, "mid": v(118.83, 6.88) * mm, "end": v(117.03, 7.62) * mm});
            skPoint(sketch, "E116.visualSharp", {"position": v(119.57, -7.62) * mm});
            skArc(sketch, "E116.filletArc", {"start": v(117.03, -7.62) * mm, "mid": v(118.83, -6.88) * mm, "end": v(119.57, -5.08) * mm});
            skPoint(sketch, "E117.visualSharp", {"position": v(2.35, -7.62) * mm});
            skArc(sketch, "E117.filletArc", {"start": v(2.35, -5.08) * mm, "mid": v(3.1, -6.88) * mm, "end": v(4.89, -7.62) * mm});
            skSolve(sketch);
        }
        {
            var Q0;
            Q0=makeQuery(id+"F24.imprint","IMPRINT",FACE,{"disambiguationData":[TD([[makeQuery(id+"F24.imprint","IMPRINT",EDGE,{"derivedFrom":sQuery(id+"F24.wireOp",EDGE,"E111")}),1.0]])]});
            var Q1;
            Q1=makeQuery(id+"F24.imprint","IMPRINT",FACE,{"disambiguationData":[TD([[makeQuery(id+"F24.imprint","IMPRINT",EDGE,{"derivedFrom":sQuery(id+"F24.wireOp",EDGE,"E108.rect.bottom")}),-1.0]])]});
            var Q2;
            Q2=makeQuery(id+"F24.imprint","IMPRINT",FACE,{"disambiguationData":[TD([[makeQuery(id+"F24.imprint","IMPRINT",EDGE,{"derivedFrom":sQuery(id+"F24.wireOp",EDGE,"E113.0.MirrorC")}),-1.0]])]});
            extrude(context, id + "F25", {"entities" : qUnion([Q0, Q1, Q2]), "operationType" : NewBodyOperationType.REMOVE, "endBound" : BoundingType.THROUGH_ALL, "oppositeDirection" : true, "depth" : 25.4 * mm});
        }
    });
